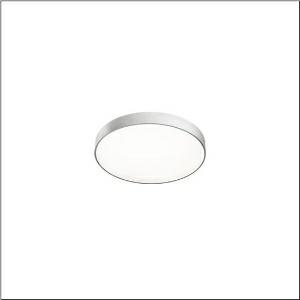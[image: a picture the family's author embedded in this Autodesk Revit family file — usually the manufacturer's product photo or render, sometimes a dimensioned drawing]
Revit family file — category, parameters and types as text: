
# Revit family: round_21_s_51mr34fd0421s
name_source: partatom
category: Lighting Fixtures
units: mm (PartAtom-declared; Revit-internal decimal feet)

## family parameters
Cut with Voids When Loaded = No
Host = Face
Light Source = No
Part Type = Normal
Room Calculation Point = No
Round Connector Dimension = Use Diameter
Shared = No

## types (1)
- Round 21 S (1 x LED, 3910 lm, 30.3 W, 4000K)
    Apparent Load = 30 VA
    CIE Flux Codes = 49 80 96 100 100
    Color Rendering = 80
    Color Temperature = 4000K
    Default Elevation = 1800 mm
    Description = Round 21 S, wall and ceiling luminaire, primary optical cover: cover, of PMMA, opal, light emission: direct distribution, primary light characteristic: symmetric, installation type: suspended mounting, surface-mounted, LED, rated luminous flux: 3.900lm, luminous efficacy: 129lm/W, light colour: 840, colour temperature: 4000K, control gear: DALI 2, with terminal, 5-pole, mains connection: 230V, AC, 50/60Hz, rated input power: 30.3W, housing, of aluminium, coated, silver, diameter: 400mm, height: 62mm, protection rating (complete): IP40, insulation class (complete): insulation class I (protective earthing), certification: CE, impact resistance: IK04, permissible operating ambient temperature: -10..+35°C, packaging unit: 1 piece
    Height = 87 mm
    Lamp = 1 x LED
    Lamp Light Flux = 3910 lm
    Lamp Power = 30.3 W
    Lamp count = 1
    Length = 400 mm
    Luminous efficacy = 129 lm/W
    Manufacturer = Siteco
    ModVariant = No
    Model = 51MR34FD0421S
    Mounting Place = Ceiling
    Mounting Type = Surface mounted
    Number of Poles = 1
    OnlyDefault = Yes
    Power Factor = 1
    Product Name = Round 21 S
    Product group = wall and ceiling luminaire
    ProductGroupID = 304
    Protection Class = Protection class I
    Protection Degree = IP 40
    RLX_Detail_Level = 1
    RLX_Emergency_Light_Flux = 0 lm
    RLX_Emergency_Type = 0
    RLX_Emergency_Type_DB = No
    RlxData = <blob elided: 11141 chars, md5=d37ef864>
    Socket = socket
    Standby Power = 0 W
    System Light Flux = 3910 lm
    System Power = 30 W
    Type Comments = Product without accessories
    Type Image = l_1258309.jpg
    URL = http://relux.com
    VarID = ---
    Voltage = 0 V
    Weight = 0.00 kg
    Width = 0 mm  [stored 0 ft]

note: [stored X ft] marks values corroborated as IEEE doubles in the binary element streams (Revit-internal decimal feet)

## geometry (parser evidence)
native form markers: Sweep x8
no freeform markers — native parametric forms only
